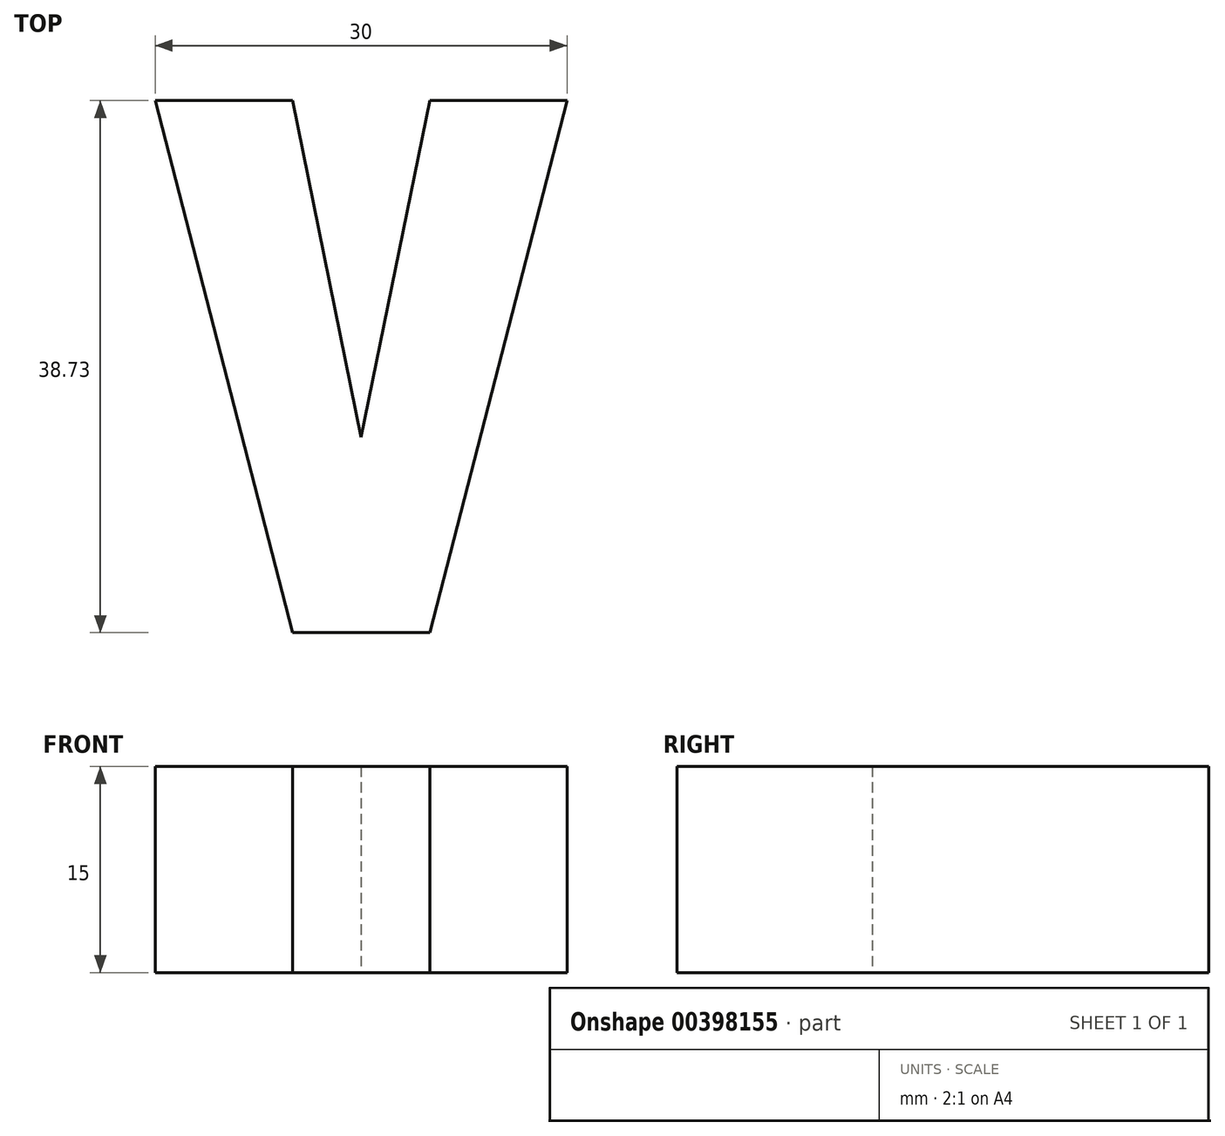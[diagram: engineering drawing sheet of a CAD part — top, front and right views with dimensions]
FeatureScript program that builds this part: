
annotation { "Feature Type Name" : "Feature", "Feature Type Description" : "" }
export const myFeature = defineFeature(function(context is Context, id is Id, definition is map)
    precondition{}
    {
        {
            var Q0;
            Q0=qCreatedBy(makeId("Top.planeOp"),FACE);
            var sketch = newSketch(context, id + "F0", { "sketchPlane" : qUnion([Q0])});
            skLineSegment(sketch, "E0", {"start": v(0, 0) * mm, "end": v(-5, 0) * mm});
            skLineSegment(sketch, "E1", {"start": v(-5, 0) * mm, "end": v(-15, 38.73) * mm});
            skLineSegment(sketch, "E2", {"start": v(-15, 38.73) * mm, "end": v(-5, 38.73) * mm});
            skLineSegment(sketch, "E3", {"start": v(-5, 38.73) * mm, "end": v(0, 14.23) * mm});
            skLineSegment(sketch, "E4", {"start": v(0, 14.23) * mm, "end": v(5, 38.73) * mm});
            skLineSegment(sketch, "E5", {"start": v(5, 38.73) * mm, "end": v(15, 38.73) * mm});
            skLineSegment(sketch, "E6", {"start": v(15, 38.73) * mm, "end": v(5, 0) * mm});
            skLineSegment(sketch, "E7", {"start": v(5, 0) * mm, "end": v(0, 0) * mm});
            skLineSegment(sketch, "E8", {"start": v(0, 0) * mm, "end": v(5, 0) * mm});
            skLineSegment(sketch, "E9", {"start": v(5, 38.73) * mm, "end": v(0, 14.23) * mm});
            skSolve(sketch);
        }
        {
            var Q0;
            Q0 = qSketchRegion(id + "F0", true);
            extrude(context, id + "F1", {"entities" : qUnion([Q0]), "depth" : 15 * mm});
        }
    });
